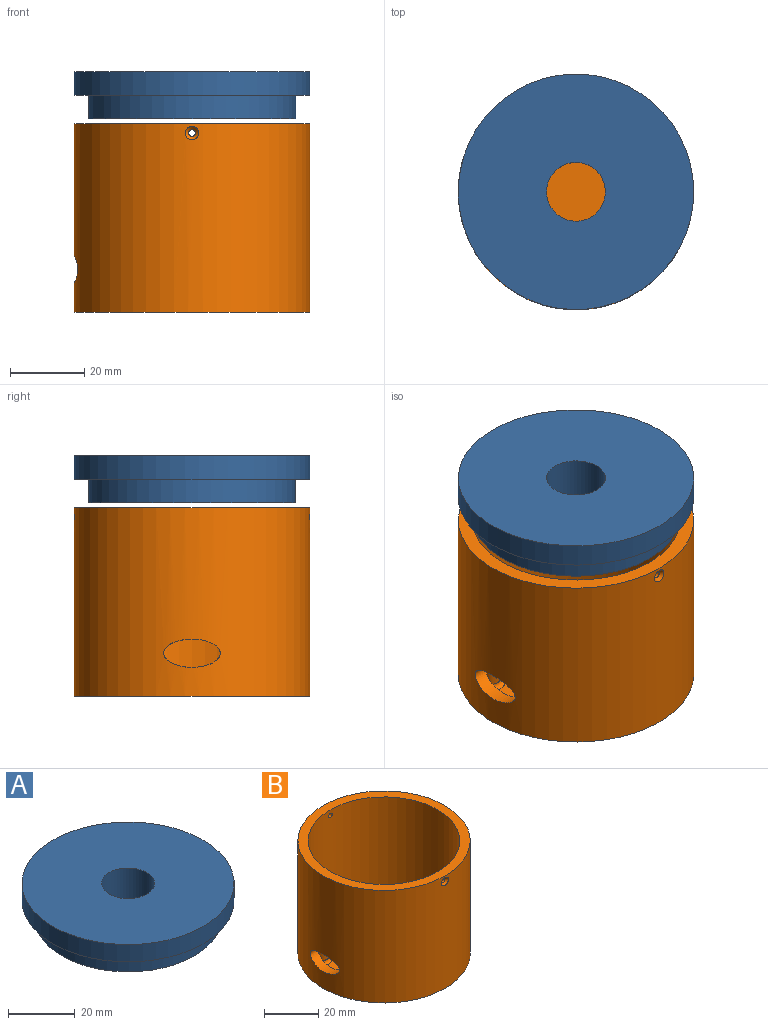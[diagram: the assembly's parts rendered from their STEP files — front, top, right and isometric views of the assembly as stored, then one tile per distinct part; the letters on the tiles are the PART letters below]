
ASSEMBLY  parts=2 mates=1
PART A: 6 faces, bbox 63.5x63.5x12.7 mm
  f0: cylinder r=31.75mm len=63.5mm, axis (0,0,-1), area 1266.8mm2, adj f1,f2
  f1: plane 63.5x63.5mm, normal (0,0,1), area 2969mm2, adj f0,f5
  f2: plane 63.5x63.5mm, normal (0,0,-1), area 714.5mm2, adj f0,f3
  f3: cylinder r=27.94mm len=55.88mm, axis (0,0,1), area 1114.8mm2, adj f2,f4
  f4: plane 55.88x55.88mm, normal (0,0,-1), area 2254.5mm2, adj f3,f5
  f5: cylinder r=7.94mm len=15.88mm, axis (0,0,1), area 633.4mm2, adj f1,f4
PART B: 31 faces, bbox 63.5x63.5x50.8 mm
  f0: cylinder r=31.75mm len=63.5mm, axis (0,0,-1), area 10022.5mm2, adj f1,f2,f26,f29,f30
  f1: plane 63.5x63.5mm, normal (0,0,1), area 714.5mm2, adj f0,f3
  f2: plane 63.5x63.5mm, normal (0,0,-1), area 3166.9mm2, adj f0
  f3: cylinder r=27.94mm len=55.88mm, axis (0,0,-1), area 7927.7mm2, adj f1,f24,f26,f27,f28
  f4: plane 53.34x53.34mm, normal (0,0,1), area 2090.3mm2, adj f21,f22,f23,f24,f25
  f5: cylinder r=1.21mm len=5.08mm, axis (0,0,-1), area 38.5mm2, adj f7,f8
  f6: cylinder r=2.54mm len=5.08mm, axis (0,0,-1), area 60.8mm2, adj f7,f21
  f7: plane 5.08x5.08mm, normal (0,0,1), area 15.7mm2, adj f5,f6
  f8: plane 2.41x2.41mm, normal (0,0,1), area 4.6mm2, adj f5
  f9: cylinder r=1.21mm len=5.08mm, axis (0,0,-1), area 38.5mm2, adj f11,f12
  f10: cylinder r=2.54mm len=5.08mm, axis (0,0,-1), area 60.8mm2, adj f11,f22
  f11: plane 5.08x5.08mm, normal (0,0,1), area 15.7mm2, adj f9,f10
  f12: plane 2.41x2.41mm, normal (0,0,1), area 4.6mm2, adj f9
  f13: cylinder r=1.21mm len=5.08mm, axis (0,0,-1), area 38.5mm2, adj f15,f16
  f14: cylinder r=2.54mm len=5.08mm, axis (0,0,-1), area 60.8mm2, adj f15,f25
  f15: plane 5.08x5.08mm, normal (0,0,1), area 15.7mm2, adj f13,f14
  f16: plane 2.41x2.41mm, normal (0,0,1), area 4.6mm2, adj f13
  f17: cylinder r=1.21mm len=5.08mm, axis (0,0,-1), area 38.5mm2, adj f19,f20
  f18: cylinder r=2.54mm len=5.08mm, axis (0,0,-1), area 60.8mm2, adj f19,f23
  f19: plane 5.08x5.08mm, normal (0,0,1), area 15.7mm2, adj f17,f18
  f20: plane 2.41x2.41mm, normal (0,0,1), area 4.6mm2, adj f17
  f21: torus R=3.81mm, axis (0,0,1), area 32.1mm2, adj f4,f6,f24
  f22: torus R=3.81mm, axis (0,0,1), area 32.1mm2, adj f4,f10,f24
  f23: torus R=3.81mm, axis (0,0,1), area 32.3mm2, adj f4,f18,f24
  f24: torus R=26.67mm, axis (0,0,1), area 325.4mm2, adj f3,f4,f21,f22,f23,f25
  f25: torus R=3.81mm, axis (0,0,1), area 32.3mm2, adj f4,f14,f24
  f26: extruded ~15.24x7.62mm, area 140.6mm2, adj f0,f3
  f27: cylinder r=0.89mm len=2.92mm, axis (0,-1,0), area 16.3mm2, adj f3,f30
  f28: cylinder r=0.89mm len=2.92mm, axis (0,-1,0), area 16.3mm2, adj f3,f29
  f29: bspline ~3.66x3.56mm, area 10.8mm2, adj f0,f28
  f30: bspline ~3.66x3.56mm, area 10.8mm2, adj f0,f27
PLACE A t=(0.39,0.15,20.52)mm
PLACE B t=(0.39,0.15,-37.9)mm
MATE parallel A.f0 <-> B.f0  axis (0,0,-1) through (0.39,0.15,20.52)mm
